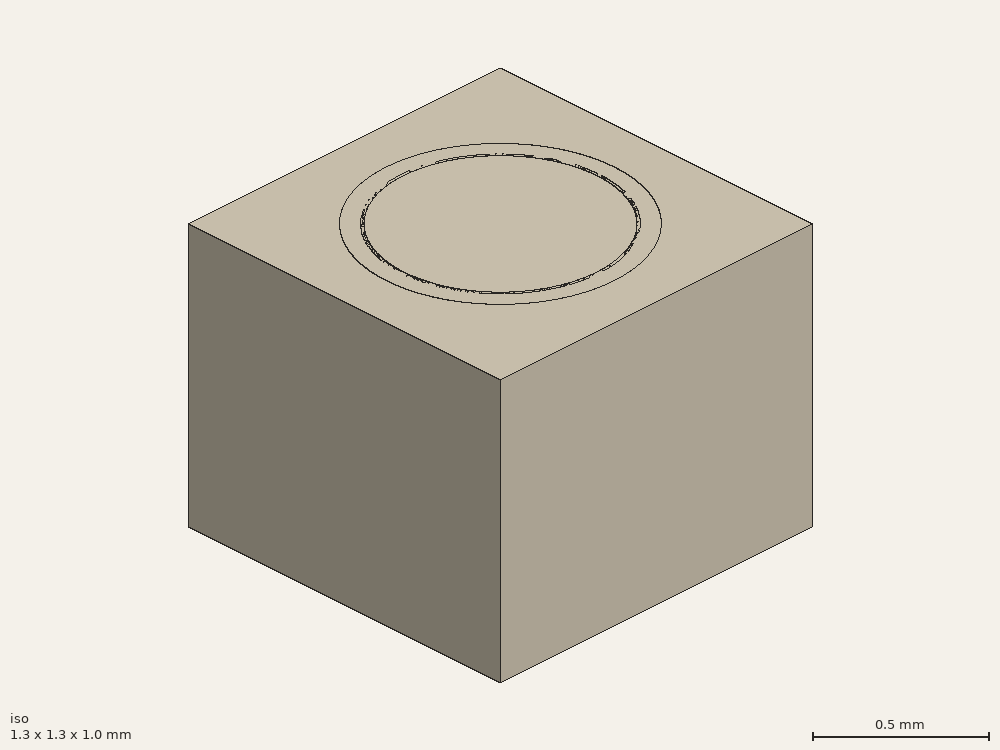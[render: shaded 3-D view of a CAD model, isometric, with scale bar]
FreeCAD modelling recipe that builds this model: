
FCSTD DOCUMENT  (FreeCAD 0.18RUnknown)
Label: PinCellOpenMC
License: All rights reserved
LicenseURL: http://en.wikipedia.org/wiki/All_rights_reserved
objects: Part::Cylinder×6, Part::Cut×3, Part::Box×1
note: 10 computed .brp shape members not serialized (recipe doc carries the construction recipe); baked Part::Feature solids carry a one-line shape summary decoded from their .brp

FEATURE [Part::Cylinder] Cylinder  label="fuel_region"
  Angle = 360
  AttacherType = Attacher::AttachEngine3D
  Height = 1
  Placement = pos=(0,0,-0.5) rot=(0,0,1;0rad)
  Radius = 0.39
FEATURE [Part::Cylinder] Cylinder001  label="clad_ir"
  Angle = 360
  AttacherType = Attacher::AttachEngine3D
  Height = 1
  Placement = pos=(0,0,-0.5) rot=(0,0,1;0rad)
  Radius = 0.4
FEATURE [Part::Cylinder] Cylinder002  label="clad_or"
  Angle = 360
  AttacherType = Attacher::AttachEngine3D
  Height = 1
  Placement = pos=(0,0,-0.5) rot=(0,0,1;0rad)
  Radius = 0.46
FEATURE [Part::Cylinder] Cylinder003  label="fuel_region001"
  Angle = 360
  AttacherType = Attacher::AttachEngine3D
  Height = 1
  Placement = pos=(0,0,-0.5) rot=(0,0,1;0rad)
  Radius = 0.39
FEATURE [Part::Cut] Cut  label="gap region"
  Base = -> Cylinder001
  Tool = -> Cylinder
FEATURE [Part::Cylinder] Cylinder004  label="fuel region"
  Angle = 360
  AttacherType = Attacher::AttachEngine3D
  Height = 1
  Placement = pos=(0,0,-0.5) rot=(0,0,1;0rad)
  Radius = 0.39
FEATURE [Part::Cut] Cut001  label="clad region"
  Base = -> Cylinder002
  Tool = -> Cylinder003
FEATURE [Part::Box] Box  label="Water Region"
  AttacherType = Attacher::AttachEngine3D
  Height = 1
  Length = 1.26
  Placement = pos=(-0.63,-0.63,-0.5) rot=(0,0,1;0rad)
  Width = 1.26
FEATURE [Part::Cylinder] Cylinder005  label="clad_or001"
  Angle = 360
  AttacherType = Attacher::AttachEngine3D
  Height = 1
  Placement = pos=(0,0,-0.5) rot=(0,0,1;0rad)
  Radius = 0.46
FEATURE [Part::Cut] Cut002  label="water region"
  Base = -> Box
  Tool = -> Cylinder005
